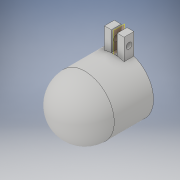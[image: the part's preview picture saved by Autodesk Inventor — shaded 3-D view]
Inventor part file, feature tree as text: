
AUTODESK INVENTOR PART (.ipt)
format: ipt  version: 2018 (Build 220112000, 112)  size: 176,640 bytes
history: native  units: in
note: dims shown in document units (in); Inventor stores cm internally (conversion verified against a paired STEP export)
features: sketch x4, extrude x2, plane x2, revolve x2
ambient origin geometry x8: Origin, YZ Plane, XZ Plane, XY Plane, X Axis, Y Axis, Z Axis, Center Point
bodies: Solid1 (feature_tree)
feature tree (10):
  extrude  "Extrusion1"  Depth=0.1969in TaperAngle=0.0deg
  extrude  "Extrusion4"  Depth=0.1969in
  plane  "Work Plane1"
  plane  "Work Plane2"
  revolve  "Revolution3"  [1 undecoded]
  revolve  "Revolution4"  [1 undecoded]
  sketch  "Sketch1"  dims[d1=0.6299in d4=0.0787in d16=0.1969in d17=0.0in]
  sketch  "Sketch4"  dims[d23=0.9449in d30=0.1969in]
  sketch  "Sketch14"  dims[d31=0.1181in d32=0.3937in d33=0.0in]
  sketch  "Sketch15"  dims[d36=-0.1969in d46=0.0591in d49=-0.1969in d61=0.9843in d62=0.5906in d63=0.0984in d64=0.5906in d65=90.0deg d67=1.1811in d68=90.0deg]
note: 2 required parameter values undecoded (feature->parameter linkage not recoverable at this tier; creation-order binding heuristic only, values carry confidence <= 0.55)
